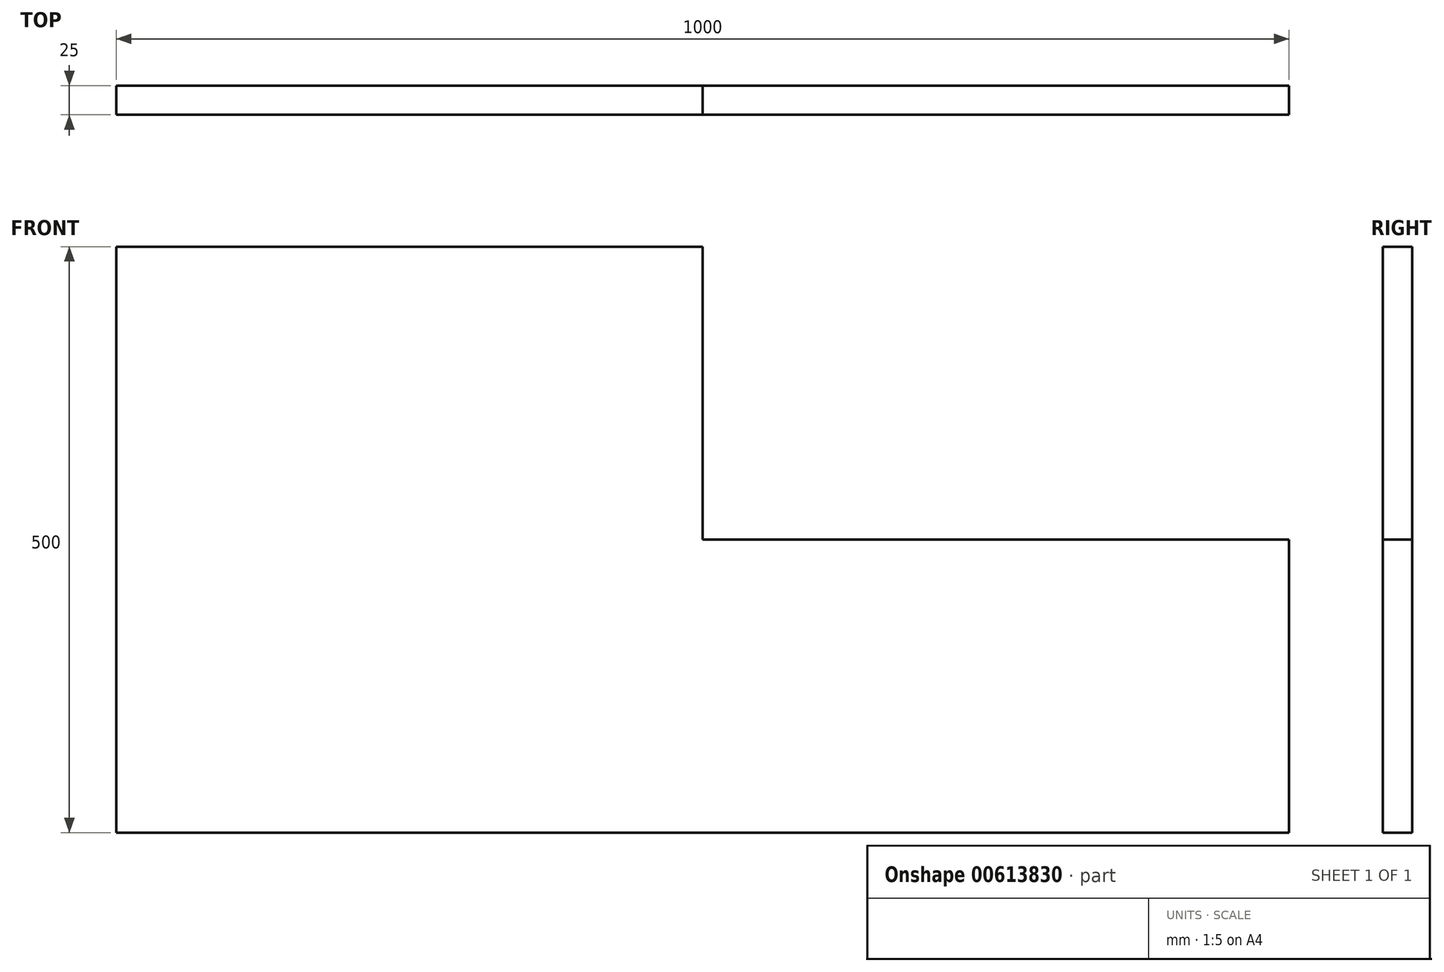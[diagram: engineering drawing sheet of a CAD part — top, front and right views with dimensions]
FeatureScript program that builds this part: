
annotation { "Feature Type Name" : "Feature", "Feature Type Description" : "" }
export const myFeature = defineFeature(function(context is Context, id is Id, definition is map)
    precondition{}
    {
        {
            var Q0;
            Q0=qCreatedBy(makeId("Front.planeOp"),FACE);
            var sketch = newSketch(context, id + "F0", { "sketchPlane" : qUnion([Q0])});
            skLineSegment(sketch, "E0", {"start": v(0, 0) * mm, "end": v(-1000, 0) * mm});
            skLineSegment(sketch, "E1", {"start": v(-1000, 0) * mm, "end": v(-1000, 500) * mm});
            skLineSegment(sketch, "E2", {"start": v(-1000, 500) * mm, "end": v(-500, 500) * mm});
            skLineSegment(sketch, "E3", {"start": v(-500, 500) * mm, "end": v(-500, 250) * mm});
            skLineSegment(sketch, "E4", {"start": v(-500, 250) * mm, "end": v(0, 250) * mm});
            skLineSegment(sketch, "E5", {"start": v(0, 250) * mm, "end": v(0, 0) * mm});
            skSolve(sketch);
        }
        {
            var Q0;
            Q0 = qSketchRegion(id + "F0", true);
            extrude(context, id + "F1", {"entities" : qUnion([Q0]), "depth" : 25 * mm, "offsetDistance" : 25 * mm});
        }
    });
